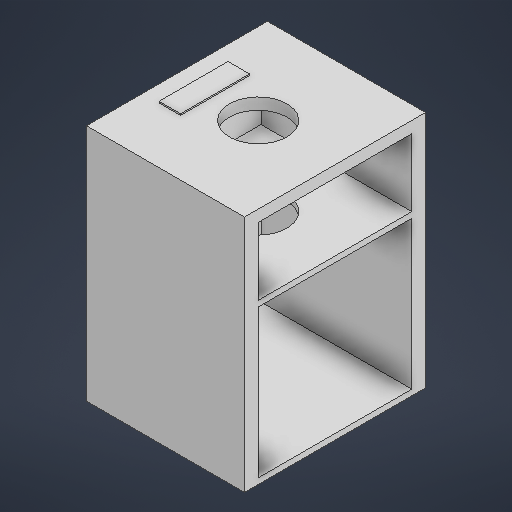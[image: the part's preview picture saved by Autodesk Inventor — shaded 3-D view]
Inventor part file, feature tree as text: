
AUTODESK INVENTOR PART (.ipt)
format: ipt  version: 2025.1 (Build 291241020, 241B)  size: 278,528 bytes
history: native  units: in
note: dims shown in document units (in); Inventor stores cm internally (conversion verified against a paired STEP export)
features: extrude x6, sketch x6, projected_geometry x3
ambient origin geometry x8: Origin, YZ Plane, XZ Plane, XY Plane, X Axis, Y Axis, Z Axis, Center Point
bodies: Solid1 (feature_tree)
feature tree (15):
  extrude  "Extrusion1"  Depth=13.75in
  extrude  "Extrusion2"  Depth=0.5in
  extrude  "Extrusion3"  Depth=13.375in
  extrude  "Extrusion4"  Depth=1.1875in
  extrude  "Extrusion5"  Depth=6.875in TaperAngle=0.0deg
  extrude  "Extrusion6"  Depth=1.0in
  sketch  "Sketch1"  dims[d0=15.75in d1=13.75in]
  sketch  "Sketch2"  dims[d2=13.875in d3=0.0in d4=0.5in]
  sketch  "Sketch3"  dims[d5=0.5in d6=13.375in]
  projected_geometry  "Projected Loop1"
  sketch  "Sketch4"  dims[d7=1.1875in d8=1.1875in]
  projected_geometry  "Projected Loop2"
  sketch  "Sketch5"  dims[d9=13.125in d10=0.0in d11=6.875in d12=0.0in]
  projected_geometry  "Projected Loop3"
  sketch  "Sketch6"  dims[d13=0.5in d14=1.0in d15=13.125in d16=0.0in d17=5.0in d20=4.1875in d21=7.625in d22=0.0in d23=6.0in d24=1.875in d26=4.875in d27=4.875in d28=0.125in d29=1.5in d30=0.0in d31=0.0in d32=10.4375in]
